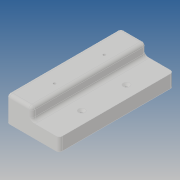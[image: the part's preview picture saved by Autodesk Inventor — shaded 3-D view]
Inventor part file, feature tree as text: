
AUTODESK INVENTOR PART (.ipt)
format: ipt  version: 2020 (Build 240168000, 168)  size: 228,864 bytes
history: native  units: in
note: dims shown in document units (in); Inventor stores cm internally (conversion verified against a paired STEP export)
features: other x7, extrude x5, sketch x5, reference x4, fillet x2, chamfer x1, projected_geometry x1
ambient origin geometry x8: Origin, YZ Plane, XZ Plane, XY Plane, X Axis, Y Axis, Z Axis, Center Point
bodies: Body1 (feature_tree)
feature tree (25):
  other  "Твердое тело1"
  extrude  "Выдавливание1"  Depth=0.1181in TaperAngle=0.0deg
  extrude  "Выдавливание2"  Depth=0.1181in TaperAngle=0.0deg
  sketch  "Эскиз3"
  other  "РабПлоскость1"
  extrude  "Выдавливание3"  Depth=0.1181in TaperAngle=0.0deg
  other  "Толщина1"
  fillet  "Сопряжение1"  Radius=0.1in
  extrude  "Выдавливание4"  Depth=0.1in
  fillet  "Сопряжение2"  Radius=0.125in
  chamfer  "Фаска1"  Distance=0.315in
  extrude  "Выдавливание5"  Depth=0.315in
  sketch  "Эскиз2"
  reference  "Ссылка1"
  reference  "Ссылка2"
  reference  "Ссылка3"
  reference  "Ссылка4"
  sketch  "Эскиз4"
  sketch  "Эскиз5"
  projected_geometry  "Спроецированная петля1"
  sketch  "Эскиз1"
  parser-record x1  (decoder bookkeeping rows leaked as tree rows — omitted from the tree; the rows remain in map.json)
  other  "realsenses_plate_v2.ipt.iam"
  other  "Intel RealSense T265:1"
  other  "body:1"
note: 1 file-system path scrubbed to <path> (originals preserved in map.json)
